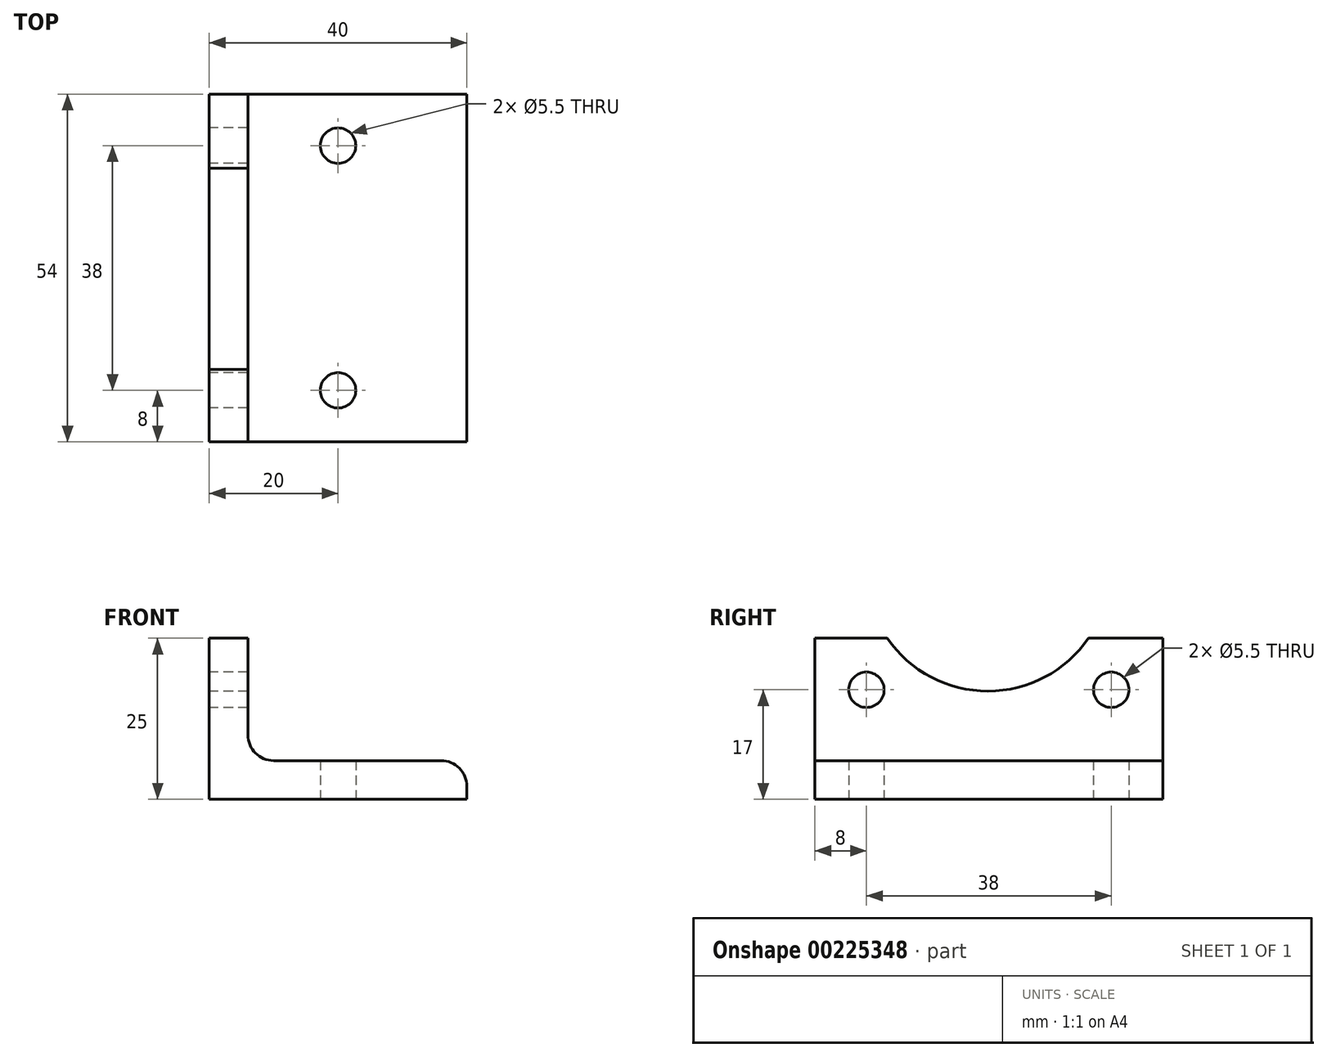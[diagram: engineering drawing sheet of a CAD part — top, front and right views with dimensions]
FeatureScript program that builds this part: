
annotation { "Feature Type Name" : "Feature", "Feature Type Description" : "" }
export const myFeature = defineFeature(function(context is Context, id is Id, definition is map)
    precondition{}
    {
        {
            var Q0;
            Q0=qCreatedBy(makeId("Front.planeOp"),FACE);
            var sketch = newSketch(context, id + "F0", { "sketchPlane" : qUnion([Q0])});
            skLineSegment(sketch, "E0", {"start": v(0, 0) * mm, "end": v(0, 25) * mm});
            skLineSegment(sketch, "E1", {"start": v(0, 0) * mm, "end": v(40, 0) * mm});
            skLineSegment(sketch, "E2", {"start": v(0, 25) * mm, "end": v(6, 25) * mm});
            skLineSegment(sketch, "E3", {"start": v(6, 25) * mm, "end": v(6, 6) * mm});
            skLineSegment(sketch, "E4", {"start": v(6, 6) * mm, "end": v(40, 6) * mm});
            skLineSegment(sketch, "E5", {"start": v(40, 6) * mm, "end": v(40, 0) * mm});
            skSolve(sketch);
        }
        {
            var Q0;
            Q0=makeQuery(id+"F0.imprint","IMPRINT",FACE,{"disambiguationData":[TD([[makeQuery(id+"F0.imprint","IMPRINT",EDGE,{"derivedFrom":sQuery(id+"F0.wireOp",EDGE,"E0")}),-1.0]])]});
            extrude(context, id + "F1", {"entities" : qUnion([Q0]), "depth" : 54 * mm});
        }
        {
            var Q0;
            Q0=makeQuery(id+"F1.opExtrude","SWEPT_EDGE",EDGE,{"disambiguationData":[OSD([sQuery(id+"F0.wireOp",EDGE,"E4"),sQuery(id+"F0.wireOp",EDGE,"E5")])]});
            fillet(context, id + "F2", {"entities" : qUnion([Q0]), "radius" : 4 * mm, "tangentPropagation" : true, "allowEdgeOverflow" : false});
        }
        {
            var Q0;
            Q0=makeQuery(id+"F1.opExtrude","SWEPT_EDGE",EDGE,{"disambiguationData":[OSD([sQuery(id+"F0.wireOp",EDGE,"E3"),sQuery(id+"F0.wireOp",EDGE,"E4")])]});
            fillet(context, id + "F3", {"entities" : qUnion([Q0]), "radius" : 4 * mm, "tangentPropagation" : true, "allowEdgeOverflow" : false});
        }
        {
            var Q0;
            Q0=qCreatedBy(makeId("Right.planeOp"),FACE);
            var sketch = newSketch(context, id + "F4", { "sketchPlane" : qUnion([Q0])});
            skPoint(sketch, "E6", {"position": v(-8, 17) * mm});
            skPoint(sketch, "E7", {"position": v(-46, 17) * mm});
            skPoint(sketch, "E8", {"position": v(-27, 36) * mm});
            skSolve(sketch);
        }
        {
            var Q0;
            Q0=makeQuery(id+"F1.opExtrude","SWEPT_FACE",FACE,{"disambiguationData":[OSD([sQuery(id+"F0.wireOp",EDGE,"E0")])]});
            var sketch = newSketch(context, id + "F5", { "sketchPlane" : qUnion([Q0])});
            skCircle(sketch, "E9", {"center": v(27.14, 35.8) * mm, "radius": 19 * mm});
            skSolve(sketch);
        }
        {
            var Q0;
            {var subQ0=sQuery(id+"F5.wireOp",EDGE,"E9");var subQ1=makeQuery(id+"F1.opExtrude","SWEPT_EDGE",EDGE,{"disambiguationData":[OSD([sQuery(id+"F0.wireOp",EDGE,"E0"),sQuery(id+"F0.wireOp",EDGE,"E2")])]});var subQ2=makeQuery(id+"F5.imprint","INTERSECT",VERTEX,{"disambiguationData":[OD(0.0)],"derivedFrom":[subQ1,subQ0]});Q0=makeQuery(id+"F5.imprint","IMPRINT",FACE,{"disambiguationData":[TD([[makeQuery(id+"F5.imprint","IMPRINT",EDGE,{"disambiguationData":[TD([[subQ2,1.0]])],"derivedFrom":subQ0}),1.0]])]});}
            var Q1;
            {var subQ0=sQuery(id+"F5.wireOp",EDGE,"E9");var subQ1=makeQuery(id+"F1.opExtrude","SWEPT_EDGE",EDGE,{"disambiguationData":[OSD([sQuery(id+"F0.wireOp",EDGE,"E0"),sQuery(id+"F0.wireOp",EDGE,"E2")])]});var subQ2=makeQuery(id+"F5.imprint","INTERSECT",VERTEX,{"disambiguationData":[OD(0.0)],"derivedFrom":[subQ1,subQ0]});Q1=makeQuery(id+"F5.imprint","IMPRINT",FACE,{"disambiguationData":[TD([[makeQuery(id+"F5.imprint","IMPRINT",EDGE,{"disambiguationData":[TD([[subQ2,-1.0]])],"derivedFrom":subQ0}),1.0]])]});}
            extrude(context, id + "F6", {"entities" : qUnion([Q0, Q1]), "operationType" : NewBodyOperationType.REMOVE, "oppositeDirection" : true, "depth" : 30 * mm});
        }
        {
            var Q0;
            Q0=sQuery(id+"F4.wireOp",VERTEX,"E6");
            var Q1;
            Q1=sQuery(id+"F4.wireOp",VERTEX,"E7");
            var Q2;
            Q2=makeQuery(id+"F1.opExtrude","SWEPT_BODY",BODY,{"disambiguationData":[OSD([sQuery(id+"F0.wireOp",EDGE,"E0"),sQuery(id+"F0.wireOp",EDGE,"E1"),sQuery(id+"F0.wireOp",EDGE,"E2"),sQuery(id+"F0.wireOp",EDGE,"E3"),sQuery(id+"F0.wireOp",EDGE,"E4"),sQuery(id+"F0.wireOp",EDGE,"E5")])]});
            hole(context, id + "F7", {"style" : HoleStyle.SIMPLE, "endStyle" : HoleEndStyle.BLIND, "oppositeDirection" : true, "holeDiameter" : 5.5 * mm, "holeDepth" : 25 * mm, "startFromSketch" : true, "locations" : qUnion([Q0, Q1]), "scope" : qUnion([Q2])});
        }
        {
            var Q0;
            Q0=qCreatedBy(makeId("Top.planeOp"),FACE);
            var sketch = newSketch(context, id + "F8", { "sketchPlane" : qUnion([Q0])});
            skPoint(sketch, "E10", {"position": v(20, -46) * mm});
            skPoint(sketch, "E11", {"position": v(20, -8) * mm});
            skSolve(sketch);
        }
        {
            var Q0;
            Q0=sQuery(id+"F8.wireOp",VERTEX,"E10");
            var Q1;
            Q1=sQuery(id+"F8.wireOp",VERTEX,"E11");
            var Q2;
            Q2=makeQuery(id+"F1.opExtrude","SWEPT_BODY",BODY,{"disambiguationData":[OSD([sQuery(id+"F0.wireOp",EDGE,"E0"),sQuery(id+"F0.wireOp",EDGE,"E1"),sQuery(id+"F0.wireOp",EDGE,"E2"),sQuery(id+"F0.wireOp",EDGE,"E3"),sQuery(id+"F0.wireOp",EDGE,"E4"),sQuery(id+"F0.wireOp",EDGE,"E5")])]});
            hole(context, id + "F9", {"style" : HoleStyle.SIMPLE, "endStyle" : HoleEndStyle.BLIND, "oppositeDirection" : true, "holeDiameter" : 5.5 * mm, "holeDepth" : 25 * mm, "startFromSketch" : true, "locations" : qUnion([Q0, Q1]), "scope" : qUnion([Q2])});
        }
    });
